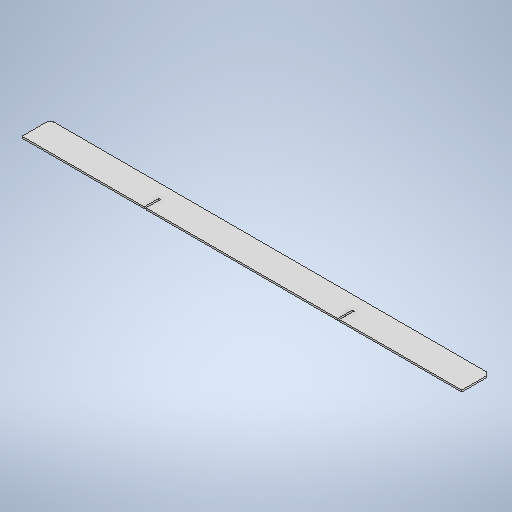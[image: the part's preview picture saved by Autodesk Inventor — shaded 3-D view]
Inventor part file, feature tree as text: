
AUTODESK INVENTOR PART (.ipt)
format: ipt  version: 2025 (Build 290162010, 162A)  size: 369,152 bytes
history: native  units: mm
features: other x5, sketch x3, sheet_metal_op x1, extrude x1
ambient origin geometry x8: Origin, YZ Plane, XZ Plane, XY Plane, X Axis, Y Axis, Z Axis, Center Point
bodies: Body1 (feature_tree)
feature tree (10):
  sheet_metal_op  "Face1"
  extrude  "Extrusion1"  Depth=780.0mm
  other  "Mark1"
  other  "A-Side Definition"
  other  "Corner Chamfer1"
  sketch  "Sketch1"  dims[d16=50.0mm d17=780.0mm]
  other  "Plate2"
  sketch  "Sketch2"  dims[d18=50.0mm]
  sketch  "Sketch4"  dims[d19=50.0mm d20=3.0mm d23=26.0mm d24=10.0mm d25=0.0mm d27=26.0mm d28=3.1mm d34=340.0mm d35=6.0mm d36=6.0mm d37=45.0deg]
  other  "Definition1"
